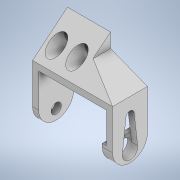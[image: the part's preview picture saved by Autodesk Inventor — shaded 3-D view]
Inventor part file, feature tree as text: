
AUTODESK INVENTOR PART (.ipt)
format: ipt  version: 2022.2 (Build 262287010, 287A)  size: 205,824 bytes
history: native  units: mm
features: extrude x8, sketch x7, fillet x1
ambient origin geometry x8: Origin, YZ Plane, XZ Plane, XY Plane, X Axis, Y Axis, Z Axis, Center Point
bodies: Solid1 (feature_tree)
feature tree (16):
  extrude  "Extrusion1"  Depth=3.0mm
  extrude  "Extrusion2"  Depth=5.0mm
  extrude  "Extrusion4"  Depth=39.0mm
  extrude  "Extrusion5"  Depth=17.0mm TaperAngle=0.0deg
  extrude  "Extrusion10"  Depth=17.0mm TaperAngle=0.0deg
  extrude  "Extrusion11"  Depth=17.0mm
  extrude  "Extrusion12"  Depth=8.5mm
  fillet  "Fillet2"  Radius=8.5mm
  extrude  "Extrusion13"  Depth=5.0mm
  sketch  "Sketch1"  dims[d0=3.0mm d1=25.0mm]
  sketch  "Sketch2"  dims[d2=5.0mm d3=25.0mm]
  sketch  "Sketch5"  dims[d4=31.0mm d5=39.0mm]
  sketch  "Sketch10"  dims[d6=17.0mm d7=17.0mm d8=0.0mm]
  sketch  "Sketch11"  dims[d9=14.0mm d10=17.0mm d11=0.0mm]
  sketch  "Sketch12"  dims[d17=17.0mm d18=7.0mm]
  sketch  "Sketch13"  dims[d19=7.0mm d20=8.5mm d22=8.5mm d23=5.0mm d24=14.0mm d25=0.0mm d26=3.0mm d27=3.0mm d28=14.0mm d29=0.0mm d48=5.0mm d49=20.0mm d50=18.0mm d51=7.0mm d52=10.0mm d53=0.0mm d54=7.5mm d55=5.0mm d56=8.5mm d57=10.0mm d58=0.0mm d59=5.0mm d60=5.0mm d61=8.5mm d62=10.0mm d63=0.0mm d64=8.5mm d65=4.0mm d66=15.0mm d67=0.0mm d68=3.0mm d69=0.0mm d70=2.0mm d71=15.0mm]
